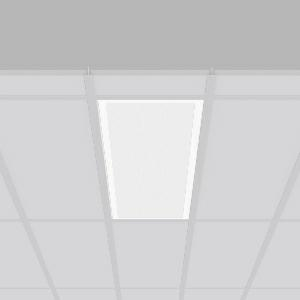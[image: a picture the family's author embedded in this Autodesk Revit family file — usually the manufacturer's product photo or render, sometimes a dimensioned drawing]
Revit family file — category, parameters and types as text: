
# Revit family: sidelite_eco_672374_002_07_e545
name_source: partatom
category: Lighting Fixtures
units: mm (PartAtom-declared; Revit-internal decimal feet)

## family parameters
Cut with Voids When Loaded = No
Host = Face
Light Source = No
Part Type = Normal
Room Calculation Point = No
Round Connector Dimension = Use Diameter
Shared = No

## types (1)
- SIDELITE ECO (1 x LED Modul 830, 3150 lm, 3000)
    Apparent Load = 29 VA
    CIE Flux Codes = 60 87 97 100 100
    Color Rendering = 80
    Color Temperature = 3000
    Default Elevation = 1800 mm
    Description = Series: SIDELITE ECO
Highly economical recessed luminaire with progressive LED technology. For escape route illumination. Frame made of aluminium, powder-coated. Diffuser plastic microprismatic. Lightguide and diffuser made of non-yellowing plastic (PMMA). Lateral light emission (RZB SIDELITE technology) for homogeneous light distribution. External driver. Self-contained system with automatic self-test and feedback via DALI bus, only to RZB DALI monitoring system. External driver with simple plug-in locking system. Extended connection cable (1.90 m). 
Colour: white
Length: 1245 mm
Width: 308 mm
Cut-out length: 1220 mm
Cut-out width: 285 mm
Recess height: 160 mm
Luminaire: recess height: 40 mm
Weight: 4.7 kg
Operating mode: maintained power mode
Duration time: 3 h
Lamp: LED
Socket: without socket
Colour temperature: 3000K
Colour rendering index (CRI): 80
System power: 29 W
Rated luminous flux: 3150 lm
Luminous flux, emergency: 460 lm
System power, emergency: -
Control gear: Regulated power supply
Protection class: I
Type of protection: IP 40
    Height = 0 mm  [stored 0 ft]
    Lamp = 1 x LED Modul 830
    Lamp Light Flux = 3150 lm
    Lamp count = 1
    Length = 1245 mm
    Lifetime = 50000 h
    Luminous efficacy = 109 lm/W
    Manufacturer = RZB
    ModVariant = No
    Model = 672374.002.07
    Mounting Place = Ceiling
    Mounting Type = Recessed
    Number of Poles = 1
    OnlyDefault = Yes
    Power Factor = 1
    Product Name = SIDELITE ECO
    Product group = Recessed modular luminaires
    ProductGroupID = 406
    Protection Class = Protection class I
    Protection Degree = IP 40
    RLX_Detail_Level = 1
    RLX_Emergency_Light_Flux = 460 lm
    RLX_Emergency_Type = 3
    RLX_Emergency_Type_DB = Yes
    RlxData = <blob elided: 34249 chars, md5=aeceff25>
    Socket = socket
    Standby Power = 0 W
    System Light Flux = 3150 lm
    System Power = 29 W
    Type Comments = Product without accessories
    Type Image = 312368.002.jpg
    URL = http://relux.com
    VarID = ---
    Voltage = 230 V
    Voltage Range = 220-240 V
    Weight = 0.00 kg
    Width = 308 mm

note: [stored X ft] marks values corroborated as IEEE doubles in the binary element streams (Revit-internal decimal feet)

## geometry (parser evidence)
native form markers: Blend x4, Sweep x12
no freeform markers — native parametric forms only
